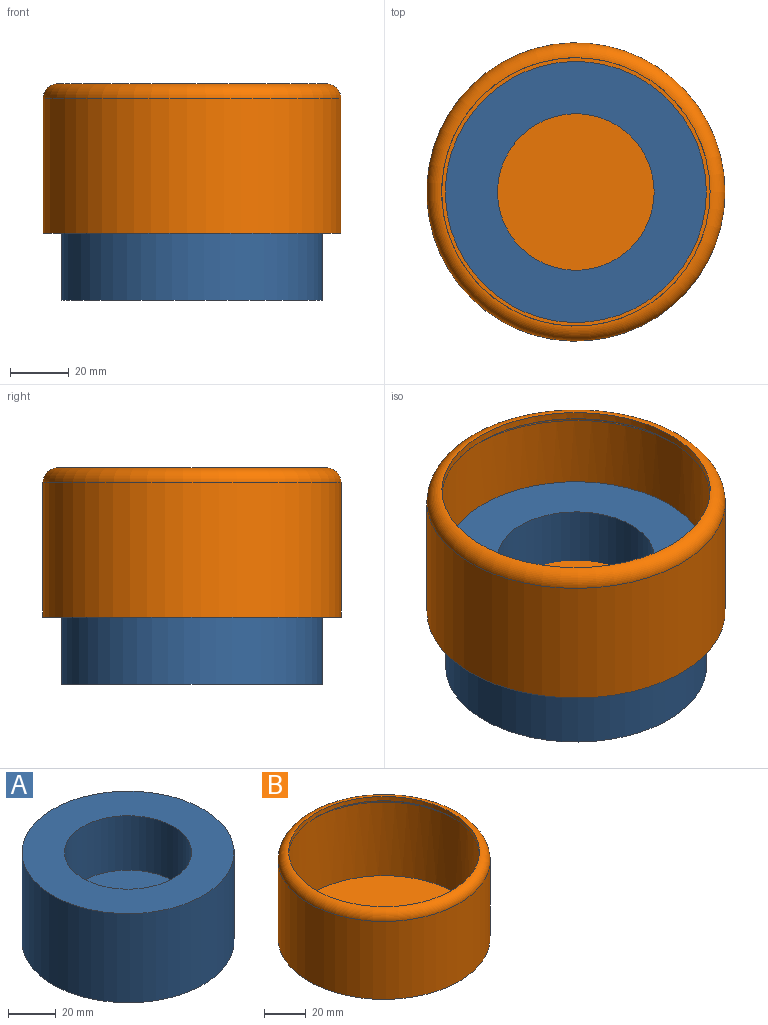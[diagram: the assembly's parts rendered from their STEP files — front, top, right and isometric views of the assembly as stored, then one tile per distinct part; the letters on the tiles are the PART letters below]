
ASSEMBLY  parts=2 mates=2
PART A: 5 faces, bbox 88.9x88.9x45.7 mm
  f0: cylinder r=44.45mm len=88.9mm, axis (0,0,-1), area 12769mm2, adj f1,f2
  f1: plane 88.9x88.9mm, normal (0,0,1), area 3972.6mm2, adj f0,f3
  f2: plane 88.9x88.9mm, normal (0,0,-1), area 6207.2mm2, adj f0
  f3: cylinder r=26.67mm len=53.34mm, axis (0,0,-1), area 4682mm2, adj f1,f4
  f4: plane 53.34x53.34mm, normal (0,0,1), area 2234.6mm2, adj f3
PART B: 7 faces, bbox 110x110x50.8 mm
  f0: cylinder r=50.8mm len=101.6mm, axis (0,0,-1), area 14593.2mm2, adj f1,f2
  f1: plane 101.6x101.6mm, normal (0,0,-1), area 8107.3mm2, adj f0
  f2: torus R=45.72mm, axis (0,0,1), area 2454.4mm2, adj f0,f3
  f3: cylinder r=45.72mm len=91.44mm, axis (0,0,1), area 729.7mm2, adj f2,f6
  f4: cylinder r=48.26mm len=96.52mm, axis (0,0,-1), area 13093.3mm2, adj f5,f6
  f5: plane 96.52x96.52mm, normal (0,0,1), area 7316.9mm2, adj f4
  f6: torus R=45.72mm, axis (0,0,1), area 1186.7mm2, adj f3,f4
PLACE A t=(-23.63,-5.09,-22.61)mm
PLACE B t=(-23.63,-5.09,0.25)mm
MATE fastened A.f0 <-> B.f0  axis (0,0,1) through (-23.63,-5.09,23.11)mm
MATE slider A.f0 <-> B.f0  axis (0,0,-1) through (-23.63,-5.09,0.25)mm
